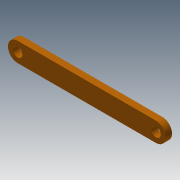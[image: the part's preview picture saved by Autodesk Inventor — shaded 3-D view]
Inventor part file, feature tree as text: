
AUTODESK INVENTOR PART (.ipt)
format: ipt  version: 2013 (Build 170138000, 138)  size: 85,504 bytes
history: native  units: mm
features: extrude x2, sketch x2
ambient origin geometry x8: Origin, YZ Plane, XZ Plane, XY Plane, X Axis, Y Axis, Z Axis, Center Point
bodies: Solid1 (feature_tree)
feature tree (4):
  extrude  "Extrusion1"  Depth=6.0mm
  extrude  "Extrusion2"  Depth=3.0mm
  sketch  "Sketch1"  dims[d0=43.0mm d1=6.0mm]
  sketch  "Sketch2"  dims[d3=2.0mm d4=0.0mm d5=3.0mm d6=3.0mm d7=2.0mm d8=0.0mm]
